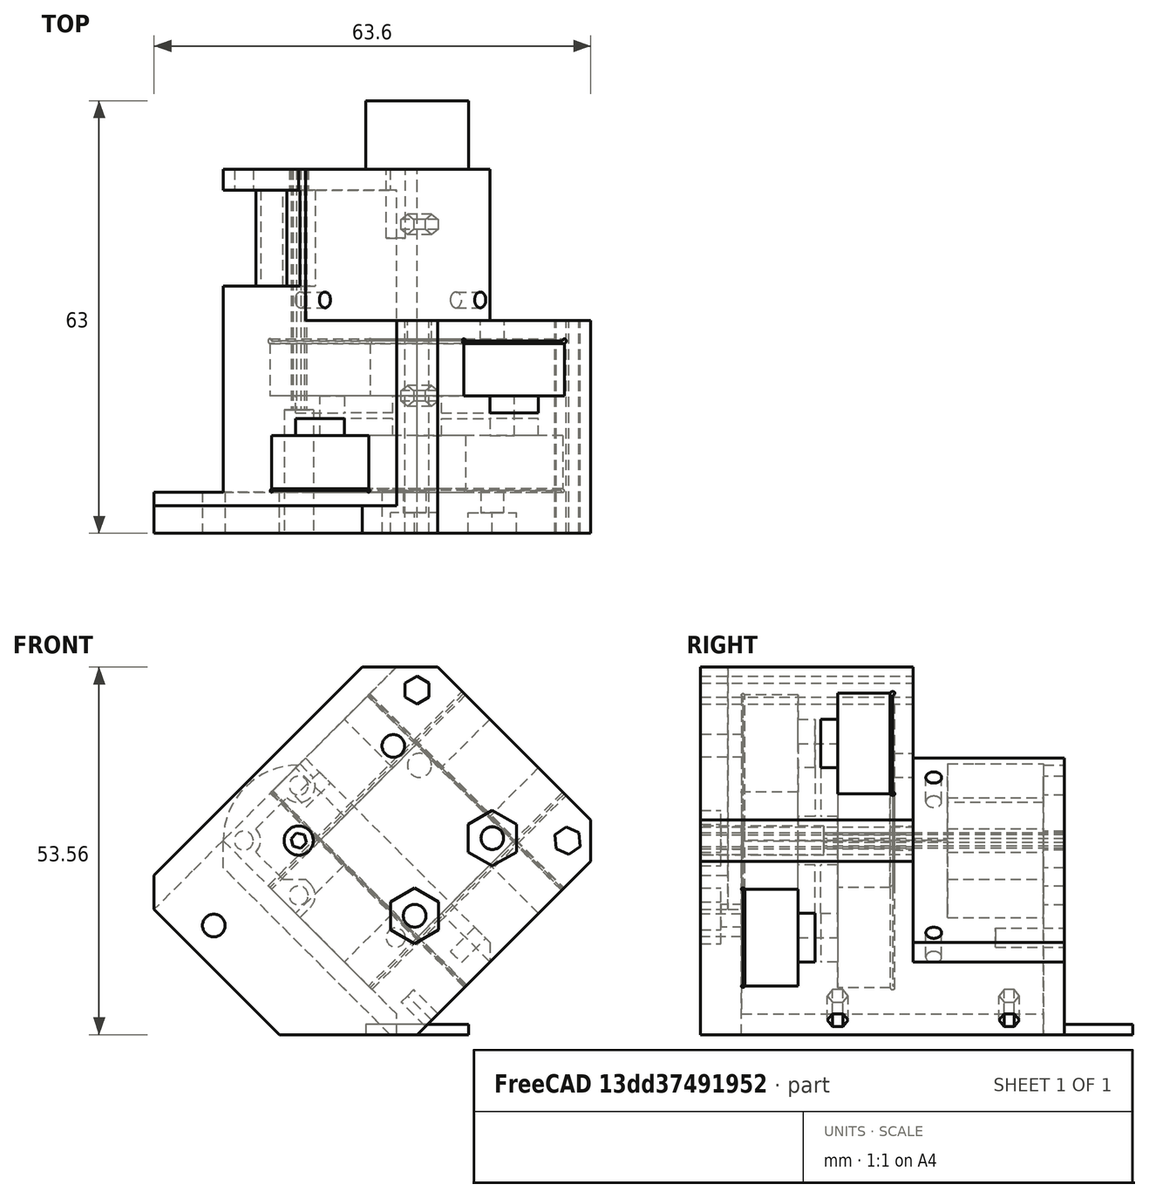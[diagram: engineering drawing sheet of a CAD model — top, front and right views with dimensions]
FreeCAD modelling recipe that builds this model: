
FCSTD DOCUMENT  (FreeCAD 0.19R)
Label: bottom
License: All rights reserved
LicenseURL: http://en.wikipedia.org/wiki/All_rights_reserved
objects: Sketcher::SketchObject×25, PartDesign::Pocket×18, PartDesign::Pad×5, PartDesign::Body×1, Mesh::Feature×1
note: 72 computed .brp shape members not serialized (recipe doc carries the construction recipe); baked Part::Feature solids carry a one-line shape summary decoded from their .brp

FEATURE [Sketcher::SketchObject] Sketch  label="Body001"
  FullyConstrained = true
  MapMode = 5
  Support = -> [XY_Plane]
  sketch-geometry (11):
    g0: LineSegment StartX=20 StartY=15.7574 StartZ=0 EndX=20 EndY=-15.7574 EndZ=0
    g1: LineSegment StartX=15.7574 StartY=-20 StartZ=0 EndX=-20 EndY=-20 EndZ=0
    g2: LineSegment StartX=-20 StartY=-15.7574 StartZ=0 EndX=-20 EndY=19.9515 EndZ=0
    g3: Circle CenterX=-12.1976 CenterY=12.1976 CenterZ=0 NormalX=0 NormalY=0 NormalZ=1 AngleXU=0 Radius=2.1
    g4: LineSegment StartX=-12.1976 StartY=12.1976 StartZ=0 EndX=0 EndY=0 EndZ=0
    g5: ArcOfCircle CenterX=-12.1976 CenterY=12.1976 CenterZ=0 NormalX=0 NormalY=0 NormalZ=1 AngleXU=0 Radius=11 StartAngle=0.788519 EndAngle=2.35931
    g6: LineSegment StartX=-4.44373 StartY=20 StartZ=0 EndX=15.7574 EndY=20 EndZ=0
    g7: LineSegment StartX=15.7574 StartY=-20 StartZ=0 EndX=20 EndY=-15.7574 EndZ=0
    g8: LineSegment StartX=-20 StartY=-15.7574 StartZ=0 EndX=-22.1213 EndY=-17.8787 EndZ=0
    g9: LineSegment StartX=-22.1213 StartY=-17.8787 StartZ=0 EndX=-20 EndY=-20 EndZ=0
    g10: LineSegment StartX=15.7574 StartY=20 StartZ=0 EndX=20 EndY=15.7574 EndZ=0
  constraints (32):
    c: Horizontal(g1)
    c: Vertical(g0)
    c: Vertical(g2)
    c: Distance(g-1,g3) = 17.25
    c: Coincident(g4,g3)
    c: Coincident(g4,g-1)
    c: Angle(g4) = -0.785398
    c: Diameter(g3) = 4.2
    c: Coincident(g5,g3)
    c: Diameter(g5) = 22
    c: DistanceX(g1) = -20
    c: Coincident(g6,g5)
    c: Horizontal(g6)
    c: Coincident(g5,g2)
    c: Coincident(g7,g1)
    c: Coincident(g7,g0)
    c: Angle(g7) = 0.785398
    c: Distance(g7) = 6
    c: DistanceY(g1) = -20
    c: Coincident(g2,g8)
    c: Coincident(g8,g9)
    c: Coincident(g9,g1)
    c: Angle(g9) = -0.785398
    c: Angle(g8) = -2.35619
    c: Distance(g9) = 3
    c: DistanceX(g2) = -20
    c: Coincident(g10,g6)
    c: Coincident(g10,g0)
    c: Distance(g10) = 6
    c: Angle(g10) = -0.785398
    c: DistanceX(g0) = 20
    c: DistanceY(g6) = 20
FEATURE [PartDesign::Pad] Pad
  Direction = (1,1,1)
  Length = 53
  Length2 = 10
  Profile = -> Sketch
  Reversed = true
  Type = 0
FEATURE [Sketcher::SketchObject] Sketch001  label="RailHole"
  FullyConstrained = true
  MapMode = 5
  Placement = pos=(20,0,0) rot=(0.57735,0.57735,0.57735;2.0944rad)
  Support = -> [Pad]
  sketch-geometry (10):
    g0: LineSegment StartX=-10.35 StartY=-27.65 StartZ=0 EndX=-10.35 EndY=-20 EndZ=0
    g1: LineSegment StartX=5 StartY=-17.5 StartZ=0 EndX=-5 EndY=-17.5 EndZ=0
    g2: LineSegment StartX=10 StartY=-28 StartZ=0 EndX=-10 EndY=-28 EndZ=0
    g3: LineSegment StartX=5 StartY=-17.5 StartZ=0 EndX=5 EndY=-20 EndZ=0
    g4: LineSegment StartX=-5 StartY=-20 StartZ=0 EndX=-5 EndY=-17.5 EndZ=0
    g5: LineSegment StartX=-10.35 StartY=-20 StartZ=0 EndX=-5 EndY=-20 EndZ=0
    g6: LineSegment StartX=5 StartY=-20 StartZ=0 EndX=10.3495 EndY=-20 EndZ=0
    g7: LineSegment StartX=10.3495 StartY=-27.65 StartZ=0 EndX=10.3495 EndY=-20 EndZ=0
    g8: ArcOfCircle CenterX=-10.35 CenterY=-28 CenterZ=0 NormalX=0 NormalY=0 NormalZ=1 AngleXU=0 Radius=0.35 StartAngle=1.5708 EndAngle=6.28319
    g9: ArcOfCircle CenterX=10.35 CenterY=-28 CenterZ=0 NormalX=0 NormalY=0 NormalZ=1 AngleXU=0 Radius=0.35 StartAngle=3.14159 EndAngle=7.85541
  constraints (29):
    c: Vertical(g0)
    c: Symmetric(g1,g1,g-2)
    c: Distance(g1) = 10
    c: Coincident(g1,g3)
    c: Vertical(g3)
    c: Coincident(g4,g1)
    c: Symmetric(g3,g4,g-2)
    c: Distance(g3) = 2.5
    c: Distance(g2) = 20
    c: Coincident(g5,g4)
    c: Horizontal(g5)
    c: Coincident(g3,g6)
    c: Horizontal(g6)
    c: Vertical(g7)
    c: Coincident(g0,g5)
    c: Coincident(g7,g6)
    c: Coincident(g0,g8)
    c: Coincident(g8,g2)
    c: Diameter(g8) = 0.7
    c: DistanceX(g0,g8) = 0
    c: DistanceY(g2,g8) = 0
    c: Coincident(g9,g2)
    c: Coincident(g9,g7)
    c: Diameter(g9) = 0.7
    c: DistanceY(g2,g9) = 0
    c: DistanceX(g7,g9) = 0.0005
    c: Symmetric(g9,g8,g-2)
    c: Distance(g9,g6) = 8
    c: DistanceY(g8) = -28
FEATURE [PartDesign::Pocket] Pocket
  BaseFeature = -> Pad
  Length = 5
  Length2 = 100
  Profile = -> Sketch001
  Type = 1
FEATURE [Sketcher::SketchObject] Sketch008  label="ExtruderHole"
  FullyConstrained = false
  MapMode = 5
  Placement = pos=(0,0,4) rot=(0,0,1;0rad)
  sketch-geometry (2):
    g0: LineSegment StartX=0 StartY=0 StartZ=0 EndX=-54.6242 EndY=54.6242 EndZ=0
    g1: Circle CenterX=-12.1976 CenterY=12.1976 CenterZ=0 NormalX=0 NormalY=0 NormalZ=1 AngleXU=0 Radius=0.75
  constraints (5):
    c: Coincident(g0,g-1)
    c: Angle(g0) = 2.35619
    c: PointOnObject(g1,g0)
    c: Distance(g-1,g1) = 17.25
    c: Diameter(g1) = 1.5
FEATURE [Sketcher::SketchObject] Sketch009  label="reference"
  FullyConstrained = false
  MapMode = 5
  Placement = pos=(0,0,-25) rot=(1,0,0;3.14159rad)
  sketch-geometry (2):
    g0: Circle CenterX=-12.0208 CenterY=-12.0208 CenterZ=0 NormalX=0 NormalY=0 NormalZ=1 AngleXU=0 Radius=10
    g1: LineSegment StartX=0 StartY=0 StartZ=0 EndX=-27.7674 EndY=-27.7674 EndZ=0
  constraints (5):
    c: Diameter(g0) = 20
    c: Coincident(g1,g-1)
    c: Angle(g1) = -2.35619
    c: PointOnObject(g0,g1)
    c: Distance(g0,g1) = 17
FEATURE [Sketcher::SketchObject] Sketch010  label="reference2"
  FullyConstrained = false
  MapMode = 5
  Placement = pos=(0,0,-37) rot=(1,0,0;3.14159rad)
  sketch-geometry (2):
    g0: Circle CenterX=-12.1976 CenterY=-12.1976 CenterZ=0 NormalX=0 NormalY=0 NormalZ=1 AngleXU=0 Radius=8
    g1: LineSegment StartX=0 StartY=0 StartZ=0 EndX=-38.1566 EndY=-38.1566 EndZ=0
  constraints (5):
    c: Diameter(g0) = 16
    c: Coincident(g1,g-1)
    c: Angle(g1) = -2.35619
    c: Distance(g0,g1) = 17.25
    c: PointOnObject(g0,g1)
FEATURE [Sketcher::SketchObject] Sketch021  label="InternalTri"
  FullyConstrained = true
  MapMode = 5
  Placement = pos=(0,-3e-15,-12) rot=(0,0,1;0rad)
  sketch-geometry (4):
    g0: LineSegment StartX=-10 StartY=10 StartZ=0 EndX=10 EndY=10 EndZ=0
    g1: LineSegment StartX=10 StartY=10 StartZ=0 EndX=10 EndY=-10 EndZ=0
    g2: LineSegment StartX=10 StartY=-10 StartZ=0 EndX=-10 EndY=-10 EndZ=0
    g3: LineSegment StartX=-10 StartY=-10 StartZ=0 EndX=-10 EndY=10 EndZ=0
  constraints (11):
    c: Coincident(g0,g1)
    c: Coincident(g1,g2)
    c: Coincident(g2,g3)
    c: Coincident(g3,g0)
    c: Horizontal(g0)
    c: Horizontal(g2)
    c: Vertical(g1)
    c: Vertical(g3)
    c: Symmetric(g1,g0,g-1)
    c: Equal(g1,g0)
    c: Distance(g1) = 20
FEATURE [PartDesign::Pocket] Pocket002
  BaseFeature = -> Pocket
  Length = 10
  Length2 = 2
  Profile = -> Sketch021
  Type = 4
FEATURE [Sketcher::SketchObject] Sketch019  label="RailHole2"
  FullyConstrained = true
  MapMode = 5
  Placement = pos=(0,-20,0) rot=(1,0,0;1.5708rad)
  Support = -> [Pocket002]
  sketch-geometry (10):
    g0: LineSegment StartX=-9.75 StartY=-6.2 StartZ=0 EndX=9.75 EndY=-6.2 EndZ=0
    g1: LineSegment StartX=10 StartY=-14.2 StartZ=0 EndX=5 EndY=-14.2 EndZ=0
    g2: LineSegment StartX=5 StartY=-14.2 StartZ=0 EndX=5 EndY=-16.7 EndZ=0
    g3: LineSegment StartX=5 StartY=-16.7 StartZ=0 EndX=-5 EndY=-16.7 EndZ=0
    g4: LineSegment StartX=-5 StartY=-16.7 StartZ=0 EndX=-5 EndY=-14.2 EndZ=0
    g5: LineSegment StartX=-5 StartY=-14.2 StartZ=0 EndX=-10 EndY=-14.2 EndZ=0
    g6: ArcOfCircle CenterX=10 CenterY=-6.2 CenterZ=0 NormalX=0 NormalY=0 NormalZ=1 AngleXU=0 Radius=0.25 StartAngle=4.71239 EndAngle=9.42478
    g7: ArcOfCircle CenterX=-10 CenterY=-6.2 CenterZ=0 NormalX=0 NormalY=0 NormalZ=1 AngleXU=0 Radius=0.25 StartAngle=-9e-16 EndAngle=4.71239
    g8: LineSegment StartX=-10 StartY=-14.2 StartZ=0 EndX=-10 EndY=-6.45 EndZ=0
    g9: LineSegment StartX=10 StartY=-14.2 StartZ=0 EndX=10 EndY=-6.45 EndZ=0
  constraints (29):
    c: Horizontal(g0)
    c: Horizontal(g1)
    c: Coincident(g1,g2)
    c: Vertical(g2)
    c: Coincident(g2,g3)
    c: Horizontal(g3)
    c: Coincident(g3,g4)
    c: Vertical(g4)
    c: Coincident(g4,g5)
    c: Symmetric(g1,g5,g-2)
    c: Distance(g3) = 10
    c: Symmetric(g4,g1,g-2)
    c: DistanceY(g0) = -6.2
    c: Distance(g2) = 2.5
    c: Coincident(g6,g0)
    c: Coincident(g7,g0)
    c: Distance(g7,g6) = 20
    c: DistanceY(g1,g6) = 8
    c: Coincident(g8,g5)
    c: Vertical(g8)
    c: Coincident(g9,g1)
    c: Coincident(g9,g6)
    c: Vertical(g9)
    c: Coincident(g7,g8)
    c: Symmetric(g6,g7,g-2)
    c: Diameter(g6) = 0.5
    c: Equal(g6,g7)
    c: DistanceX(g7,g7) = 0
    c: DistanceY(g7,g0) = 0
FEATURE [Sketcher::SketchObject] Sketch024  label="hgxLITEholes"
  FullyConstrained = false
  MapMode = 5
  Placement = pos=(0,0,4) rot=(0,0,1;0rad)
  sketch-geometry (5):
    g0: Circle CenterX=7.30241 CenterY=12.1976 CenterZ=0 NormalX=0 NormalY=0 NormalZ=1 AngleXU=0 Radius=1.65
    g1: Circle CenterX=-29.6976 CenterY=12.1976 CenterZ=0 NormalX=0 NormalY=0 NormalZ=1 AngleXU=0 Radius=1.65
    g2: LineSegment StartX=-29.6976 StartY=12.1976 StartZ=0 EndX=7.30241 EndY=12.1976 EndZ=0
    g3: LineSegment StartX=0 StartY=0 StartZ=0 EndX=-27.1729 EndY=27.1729 EndZ=0
    g4: Circle CenterX=-12.1976 CenterY=12.1976 CenterZ=0 NormalX=0 NormalY=0 NormalZ=1 AngleXU=0 Radius=1.0154
  constraints (12):
    c: Diameter(g0) = 3.3
    c: Equal(g0,g1)
    c: Coincident(g2,g1)
    c: Coincident(g2,g0)
    c: Distance(g2) = 37
    c: Coincident(g3,g-1)
    c: Angle(g3) = 2.35619
    c: PointOnObject(g4,g3)
    c: Distance(g-1,g4) = 17.25
    c: Distance(g4,g0) = 19.5
    c: Horizontal(g2)
    c: PointOnObject(g4,g2)
FEATURE [PartDesign::Pocket] Pocket003
  BaseFeature = -> Pocket002
  Length = 5
  Length2 = 100
  Profile = -> Sketch019
  Type = 1
FEATURE [Sketcher::SketchObject] Sketch026  label="BottomSculp"
  FullyConstrained = false
  MapMode = 5
  Placement = pos=(0,0,-53) rot=(1,0,0;3.14159rad)
  Support = -> [Pocket003]
  sketch-geometry (5):
    g0: LineSegment StartX=29.4648 StartY=27.8981 StartZ=0 EndX=28.2209 EndY=-23.4245 EndZ=0
    g1: LineSegment StartX=28.2209 StartY=-23.4245 StartZ=0 EndX=-3.00001 EndY=-23.4245 EndZ=0
    g2: LineSegment StartX=-3.00001 StartY=-23.4245 StartZ=0 EndX=-3 EndY=18 EndZ=0
    g3: LineSegment StartX=-3 StartY=18 StartZ=0 EndX=-14.2101 EndY=29.2101 EndZ=0
    g4: LineSegment StartX=-14.2101 StartY=29.2101 StartZ=0 EndX=29.4648 EndY=27.8981 EndZ=0
  constraints (11):
    c: Coincident(g0,g1)
    c: Horizontal(g1)
    c: Coincident(g1,g2)
    c: Angle(g2) = 1.5708
    c: Coincident(g2,g3)
    c: Angle(g3) = 2.35619
    c: Coincident(g4,g3)
    c: Coincident(g4,g0)
    c: DistanceY(g2) = 18
    c: DistanceX(g2) = -3
    c: Angle(g3) = 2.35619
FEATURE [PartDesign::Pocket] Pocket004
  BaseFeature = -> Pocket003
  Length = 22
  Length2 = 100
  Profile = -> Sketch026
  Type = 0
FEATURE [Sketcher::SketchObject] Sketch004  label="Yboltpattern"
  FullyConstrained = true
  MapMode = 5
  Placement = pos=(0,0,-31) rot=(1,0,0;3.14159rad)
  Support = -> [Pocket004]
  sketch-geometry (8):
    g0: Circle CenterX=-8 CenterY=7.5 CenterZ=0 NormalX=0 NormalY=0 NormalZ=1 AngleXU=0 Radius=1.75
    g1: Circle CenterX=8 CenterY=7.5 CenterZ=0 NormalX=0 NormalY=0 NormalZ=1 AngleXU=0 Radius=1.75
    g2: Circle CenterX=-8 CenterY=-7.5 CenterZ=0 NormalX=0 NormalY=0 NormalZ=1 AngleXU=0 Radius=1.75
    g3: Circle CenterX=8 CenterY=-7.5 CenterZ=0 NormalX=0 NormalY=0 NormalZ=1 AngleXU=0 Radius=1.75
    g4: LineSegment StartX=-8 StartY=7.5 StartZ=0 EndX=8 EndY=7.5 EndZ=0
    g5: LineSegment StartX=8 StartY=7.5 StartZ=0 EndX=8 EndY=-7.5 EndZ=0
    g6: LineSegment StartX=8 StartY=-7.5 StartZ=0 EndX=-8 EndY=-7.5 EndZ=0
    g7: LineSegment StartX=-8 StartY=-7.5 StartZ=0 EndX=-8 EndY=7.5 EndZ=0
  constraints (18):
    c: Diameter(g0) = 3.5
    c: Equal(g0,g1)
    c: Equal(g0,g2)
    c: Equal(g0,g3)
    c: Distance(g2,g0) = 15
    c: Distance(g3,g2) = 16
    c: Coincident(g4,g0)
    c: Coincident(g4,g1)
    c: Coincident(g4,g5)
    c: Coincident(g5,g3)
    c: Coincident(g5,g6)
    c: Coincident(g6,g2)
    c: Coincident(g6,g7)
    c: Coincident(g7,g4)
    c: Equal(g5,g7)
    c: Equal(g4,g6)
    c: Symmetric(g1,g2,g-1)
    c: Symmetric(g0,g1,g-2)
FEATURE [Sketcher::SketchObject] Sketch022  label="VoronHoleRelif"
  FullyConstrained = true
  MapMode = 5
  Placement = pos=(0,0,-28) rot=(0,0,1;0rad)
  Support = -> [Pocket004]
  sketch-geometry (11):
    g0: ArcOfCircle CenterX=-17.8884 CenterY=6.52425 CenterZ=0 NormalX=0 NormalY=0 NormalZ=1 AngleXU=0 Radius=2.4 StartAngle=4.71239 EndAngle=6.28319
    g1: ArcOfCircle CenterX=-6.58192 CenterY=17.8307 CenterZ=0 NormalX=0 NormalY=0 NormalZ=1 AngleXU=0 Radius=2.4 StartAngle=3.14159 EndAngle=6.28319
    g2: LineSegment StartX=-22.2684 StartY=4.12425 StartZ=0 EndX=-17.8884 EndY=4.12425 EndZ=0
    g3: LineSegment StartX=-22.2684 StartY=23.8307 StartZ=0 EndX=-4.18192 EndY=23.8307 EndZ=0
    g4: LineSegment StartX=-4.18192 StartY=23.8307 StartZ=0 EndX=-4.18192 EndY=17.8307 EndZ=0
    g5: LineSegment StartX=-22.2684 StartY=4.12425 StartZ=0 EndX=-22.2684 EndY=23.8307 EndZ=0
    g6: ArcOfCircle CenterX=-17.8172 CenterY=17.8307 CenterZ=0 NormalX=0 NormalY=0 NormalZ=1 AngleXU=0 Radius=2.4 StartAngle=4.71239 EndAngle=6.28319
    g7: LineSegment StartX=-15.4172 StartY=17.8307 StartZ=0 EndX=-8.98192 EndY=17.8307 EndZ=0
    g8: LineSegment StartX=-17.8172 StartY=9.85307 StartZ=0 EndX=-15.4884 EndY=7.52425 EndZ=0
    g9: LineSegment StartX=-15.4884 StartY=6.52425 StartZ=0 EndX=-15.4884 EndY=7.52425 EndZ=0
    g10: LineSegment StartX=-17.8172 StartY=9.85307 StartZ=0 EndX=-17.8172 EndY=15.4307 EndZ=0
  constraints (33):
    c: Horizontal(g2)
    c: Coincident(g3,g4)
    c: Tangent(g4,g1) = 1.5708
    c: Tangent(g2,g0) = -1.5708
    c: Diameter(g0) = 4.8
    c: Equal(g0,g1)
    c: Vertical(g4)
    c: Horizontal(g3)
    c: Coincident(g5,g2)
    c: Coincident(g5,g3)
    c: Vertical(g5)
    c: Distance(g2) = 4.38
    c: Distance(g4) = 6
    c: DistanceX(g1) = -6.58192
    c: DistanceY(g1) = 17.8307
    c: DistanceX(g0) = -17.8884
    c: DistanceY(g0) = 6.52425
    c: Coincident(g7,g6)
    c: Coincident(g7,g1)
    c: Horizontal(g7)
    c: Perpendicular(g1,g7)
    c: Diameter(g6) = 4.8
    c: Perpendicular(g6,g7)
    c: Angle(g8) = -0.785398
    c: Vertical(g9)
    c: Tangent(g9,g0) = -1.5708
    c: Distance(g9) = 1
    c: Coincident(g8,g9)
    c: Coincident(g10,g8)
    c: Coincident(g10,g6)
    c: Vertical(g10)
    c: Perpendicular(g6,g10)
    c: DistanceX(g6) = -17.8172
FEATURE [PartDesign::Pocket] Pocket005
  BaseFeature = -> Pocket004
  Length = 22
  Length2 = -8
  Profile = -> Sketch022
  Type = 4
FEATURE [Sketcher::SketchObject] Sketch017  label="VoronHoles3"
  FullyConstrained = true
  MapMode = 5
  Placement = pos=(0,0,-50) rot=(0,0,1;0rad)
  Support = -> [Pocket005]
  sketch-geometry (10):
    g0: Circle CenterX=-6.54074 CenterY=17.8544 CenterZ=0 NormalX=0 NormalY=0 NormalZ=1 AngleXU=0 Radius=1.375
    g1: Circle CenterX=-17.8544 CenterY=6.54074 CenterZ=0 NormalX=0 NormalY=0 NormalZ=1 AngleXU=0 Radius=1.375
    g2: Circle CenterX=-6.54074 CenterY=6.54074 CenterZ=0 NormalX=0 NormalY=0 NormalZ=1 AngleXU=0 Radius=1.375
    g3: Circle CenterX=-17.8544 CenterY=17.8544 CenterZ=0 NormalX=0 NormalY=0 NormalZ=1 AngleXU=0 Radius=1.375
    g4: LineSegment StartX=-6.54074 StartY=17.8544 StartZ=0 EndX=-6.54074 EndY=6.54074 EndZ=0
    g5: LineSegment StartX=-6.54074 StartY=6.54074 StartZ=0 EndX=-17.8544 EndY=6.54074 EndZ=0
    g6: LineSegment StartX=-17.8544 StartY=6.54074 StartZ=0 EndX=-17.8544 EndY=17.8544 EndZ=0
    g7: LineSegment StartX=-17.8544 StartY=17.8544 StartZ=0 EndX=-6.54074 EndY=17.8544 EndZ=0
    g8: LineSegment StartX=0 StartY=0 StartZ=0 EndX=-37.1726 EndY=37.1726 EndZ=0
    g9: Circle CenterX=-12.1976 CenterY=12.1976 CenterZ=0 NormalX=0 NormalY=0 NormalZ=1 AngleXU=0 Radius=0.77
  constraints (25):
    c: Coincident(g4,g0)
    c: Coincident(g4,g2)
    c: Coincident(g4,g5)
    c: Coincident(g5,g1)
    c: Coincident(g5,g6)
    c: Coincident(g6,g3)
    c: Coincident(g6,g7)
    c: Coincident(g7,g4)
    c: Equal(g4,g7)
    c: Equal(g7,g6)
    c: Equal(g6,g5)
    c: Coincident(g8,g-1)
    c: PointOnObject(g9,g8)
    c: Distance(g-1,g9) = 17.25
    c: Diameter(g1) = 2.75
    c: Equal(g1,g3)
    c: Equal(g1,g0)
    c: Equal(g1,g2)
    c: Symmetric(g0,g1,g9)
    c: Distance(g2,g3) = 16
    c: Angle(g8) = 2.35619
    c: PointOnObject(g2,g8)
    c: Perpendicular(g7,g4)
    c: Distance(g8) = 52.57
    c: Diameter(g9) = 1.54
FEATURE [PartDesign::Pocket] Pocket006
  BaseFeature = -> Pocket005
  Length = 5
  Length2 = 100
  Profile = -> Sketch017
  Type = 1
FEATURE [Sketcher::SketchObject] Sketch025  label="FanDuctMountHole"
  FullyConstrained = true
  MapMode = 5
  Placement = pos=(0,0,-53) rot=(1,0,0;3.14159rad)
  Support = -> [Pocket006]
  sketch-geometry (1):
    g0: Circle CenterX=-12.2 CenterY=7.8 CenterZ=0 NormalX=0 NormalY=0 NormalZ=1 AngleXU=0 Radius=1.4
  constraints (3):
    c: Diameter(g0) = 2.8
    c: DistanceX(g0) = -12.2
    c: DistanceY(g0) = 7.8
FEATURE [PartDesign::Pocket] Pocket007
  BaseFeature = -> Pocket006
  Length = 10
  Length2 = 100
  Profile = -> Sketch025
  Type = 0
FEATURE [PartDesign::Pocket] Pocket008
  BaseFeature = -> Pocket007
  Length = 9
  Length2 = 100
  Profile = -> Sketch004
  Type = 0
FEATURE [Sketcher::SketchObject] Sketch007  label="ExtruderPlatform"
  ExternalGeometry = -> [Pad]
  FullyConstrained = false
  MapMode = 5
  Support = -> [Pocket008]
  sketch-geometry (12):
    g0: LineSegment StartX=-20 StartY=-20 StartZ=0 EndX=15.7574 EndY=-20 EndZ=0
    g1: LineSegment StartX=0 StartY=0 StartZ=0 EndX=-70.7107 EndY=70.7107 EndZ=0
    g2: Circle CenterX=-12.1976 CenterY=12.1976 CenterZ=0 NormalX=0 NormalY=0 NormalZ=1 AngleXU=0 Radius=2.125
    g3: LineSegment StartX=15.7574 StartY=-20 StartZ=0 EndX=20 EndY=-15.7574 EndZ=0
    g4: LineSegment StartX=20 StartY=-15.7574 StartZ=0 EndX=20 EndY=15.7574 EndZ=0
    g5: LineSegment StartX=20 StartY=15.7574 StartZ=0 EndX=15.7574 EndY=20 EndZ=0
    g6: LineSegment StartX=-20 StartY=-20 StartZ=0 EndX=-34.1976 EndY=-5.80241 EndZ=0
    g7: LineSegment StartX=-12.1976 StartY=-100 StartZ=0 EndX=-12.1976 EndY=100 EndZ=0
    g8: LineSegment StartX=-34.1976 StartY=-5.80241 StartZ=0 EndX=-34.1976 EndY=20 EndZ=0
    g9: LineSegment StartX=-34.1976 StartY=20 StartZ=0 EndX=15.7574 EndY=20 EndZ=0
    g10: Circle CenterX=-29.6976 CenterY=12.1976 CenterZ=0 NormalX=0 NormalY=0 NormalZ=1 AngleXU=0 Radius=1.4
    g11: Circle CenterX=7.30241 CenterY=11.9057 CenterZ=0 NormalX=0 NormalY=0 NormalZ=1 AngleXU=0 Radius=1.4
  constraints (35):
    c: Coincident(g1,g-1)
    c: Angle(g1) = 2.35619
    c: Diameter(g2) = 4.25
    c: PointOnObject(g2,g1)
    c: Distance(g-1,g2) = 17.25
    c: Coincident(g0,g3)
    c: Coincident(g3,g4)
    c: Coincident(g6,g0)
    c: Angle(g6) = 2.35619
    c: Coincident(g5,g4)
    c: Distance(g1) = 100
    c: PointOnObject(g2,g7)
    c: DistanceX(g0,g0) = -35.7574
    c: DistanceY(g0,g0) = 0
    c: DistanceX(g3,g0) = -40
    c: DistanceY(g3,g0) = -4.24264
    c: DistanceX(g4) = 20
    c: DistanceY(g4) = 15.7574
    c: DistanceX(g3) = 20
    c: DistanceY(g3) = -15.7574
    c: Coincident(g8,g6)
    c: Vertical(g8)
    c: Horizontal(g9)
    c: Coincident(g5,g9)
    c: Distance(g8,g7) = 22
    c: DistanceX(g5) = 15.7574
    c: DistanceY(g5) = 20
    c: Symmetric(g7,g7,g-1)
    c: Distance(g7) = 200
    c: DistanceX(g10,g2) = 17.5
    c: DistanceX(g2,g11) = 19.5
    c: Diameter(g10) = 2.8
    c: Equal(g10,g11)
    c: DistanceY(g10,g2) = 0
    c: Coincident(g9,g8)
FEATURE [PartDesign::Pad] Pad001
  BaseFeature = -> Pocket008
  Direction = (1,1,1)
  Length = 6
  Length2 = 100
  Profile = -> Sketch007
  Reversed = true
  Type = 0
FEATURE [PartDesign::Pocket] Pocket009
  BaseFeature = -> Pad001
  Length = 11
  Length2 = 100
  Profile = -> Sketch024
  Type = 0
FEATURE [PartDesign::Pocket] Pocket010
  BaseFeature = -> Pocket009
  Length = 5
  Length2 = 100
  Profile = -> Sketch008
  Type = 1
FEATURE [Sketcher::SketchObject] Sketch003  label="Xboltpattern"
  FullyConstrained = true
  MapMode = 5
  Support = -> [Pocket010]
  sketch-geometry (8):
    g0: Circle CenterX=-8 CenterY=7.5 CenterZ=0 NormalX=0 NormalY=0 NormalZ=1 AngleXU=0 Radius=1.65
    g1: Circle CenterX=8 CenterY=7.5 CenterZ=0 NormalX=0 NormalY=0 NormalZ=1 AngleXU=0 Radius=1.65
    g2: Circle CenterX=-8 CenterY=-7.5 CenterZ=0 NormalX=0 NormalY=0 NormalZ=1 AngleXU=0 Radius=1.65
    g3: Circle CenterX=8 CenterY=-7.5 CenterZ=0 NormalX=0 NormalY=0 NormalZ=1 AngleXU=0 Radius=1.65
    g4: LineSegment StartX=-8 StartY=7.5 StartZ=0 EndX=8 EndY=7.5 EndZ=0
    g5: LineSegment StartX=8 StartY=7.5 StartZ=0 EndX=8 EndY=-7.5 EndZ=0
    g6: LineSegment StartX=8 StartY=-7.5 StartZ=0 EndX=-8 EndY=-7.5 EndZ=0
    g7: LineSegment StartX=-8 StartY=-7.5 StartZ=0 EndX=-8 EndY=7.5 EndZ=0
  constraints (19):
    c: Diameter(g0) = 3.3
    c: Equal(g0,g1)
    c: Equal(g0,g2)
    c: Equal(g0,g3)
    c: Distance(g0,g1) = 16
    c: Distance(g1,g3) = 15
    c: Coincident(g4,g0)
    c: Coincident(g4,g1)
    c: Horizontal(g4)
    c: Coincident(g4,g5)
    c: Coincident(g5,g3)
    c: Vertical(g5)
    c: Coincident(g5,g6)
    c: Coincident(g6,g2)
    c: Coincident(g6,g7)
    c: Coincident(g7,g4)
    c: Symmetric(g2,g1,g-1)
    c: Equal(g7,g5)
    c: Equal(g6,g4)
FEATURE [Sketcher::SketchObject] Sketch029  label="Adhesion"
  FullyConstrained = false
  MapMode = 5
  Placement = pos=(0,0,-53) rot=(1,0,0;3.14159rad)
  sketch-geometry (4):
    g0: LineSegment StartX=-13.636 StartY=24.2426 StartZ=0 EndX=-24.2426 EndY=13.636 EndZ=0
    g1: LineSegment StartX=-24.2426 StartY=13.636 StartZ=0 EndX=-25.3033 EndY=14.6967 EndZ=0
    g2: LineSegment StartX=-25.3033 StartY=14.6967 StartZ=0 EndX=-14.6967 EndY=25.3033 EndZ=0
    g3: LineSegment StartX=-14.6967 StartY=25.3033 StartZ=0 EndX=-13.636 EndY=24.2426 EndZ=0
  constraints (10):
    c: Coincident(g0,g1)
    c: Coincident(g1,g2)
    c: Coincident(g2,g3)
    c: Coincident(g3,g0)
    c: Angle(g2) = 0.785398
    c: Distance(g2) = 15
    c: Distance(g1) = 1.5
    c: Distance(g3) = 1.5
    c: Perpendicular(g2,g3)
    c: Perpendicular(g2,g1)
FEATURE [Sketcher::SketchObject] Sketch033  label="WireMgmnt"
  FullyConstrained = true
  MapMode = 5
  Placement = pos=(0,-20,0) rot=(1,0,0;1.5708rad)
  sketch-geometry (14):
    g0: LineSegment StartX=-15.7 StartY=-20.7506 StartZ=0 EndX=-15.7 EndY=-19.2494 EndZ=0
    g1: LineSegment StartX=-15.7 StartY=-19.2494 StartZ=0 EndX=-17 EndY=-18.4989 EndZ=0
    g2: LineSegment StartX=-17 StartY=-18.4989 StartZ=0 EndX=-18.3 EndY=-19.2494 EndZ=0
    g3: LineSegment StartX=-18.3 StartY=-19.2494 StartZ=0 EndX=-18.3 EndY=-20.7506 EndZ=0
    g4: LineSegment StartX=-18.3 StartY=-20.7506 StartZ=0 EndX=-17 EndY=-21.5011 EndZ=0
    g5: LineSegment StartX=-17 StartY=-21.5011 StartZ=0 EndX=-15.7 EndY=-20.7506 EndZ=0
    g6: Circle CenterX=-17 CenterY=-20 CenterZ=0 NormalX=0 NormalY=0 NormalZ=1 AngleXU=0 Radius=1.50111
    g7: LineSegment StartX=-15.7 StartY=-44.2494 StartZ=0 EndX=-17 EndY=-43.4989 EndZ=0
    g8: LineSegment StartX=-17 StartY=-43.4989 StartZ=0 EndX=-18.3 EndY=-44.2494 EndZ=0
    g9: LineSegment StartX=-18.3 StartY=-44.2494 StartZ=0 EndX=-18.3 EndY=-45.7506 EndZ=0
    g10: LineSegment StartX=-18.3 StartY=-45.7506 StartZ=0 EndX=-17 EndY=-46.5011 EndZ=0
    g11: LineSegment StartX=-17 StartY=-46.5011 StartZ=0 EndX=-15.7 EndY=-45.7506 EndZ=0
    g12: LineSegment StartX=-15.7 StartY=-45.7506 StartZ=0 EndX=-15.7 EndY=-44.2494 EndZ=0
    g13: Circle CenterX=-17 CenterY=-45 CenterZ=0 NormalX=0 NormalY=0 NormalZ=1 AngleXU=0 Radius=1.50111
  constraints (34):
    c: Coincident(g0,g1)
    c: Coincident(g1,g2)
    c: Coincident(g2,g3)
    c: Coincident(g3,g4)
    c: Coincident(g4,g5)
    c: Coincident(g5,g0)
    c: Equal(g0, g1-g5) x5
    c: PointOnObject(g0,g6)
    c: PointOnObject(g1,g6)
    c: PointOnObject(g2,g6)
    c: PointOnObject(g3,g6)
    c: PointOnObject(g4,g6)
    c: PointOnObject(g5,g6)
    c: Coincident(g7,g8)
    c: Coincident(g8,g9)
    c: Coincident(g9,g10)
    c: Coincident(g10,g11)
    c: Coincident(g11,g12)
    c: Coincident(g12,g7)
    c: Equal(g7, g8-g12) x5
    c: PointOnObject(g7,g13)
    c: PointOnObject(g8,g13)
    c: PointOnObject(g9,g13)
    c: PointOnObject(g10,g13)
    c: PointOnObject(g11,g13)
    c: PointOnObject(g12,g13)
    c: DistanceX(g13) = -17
    c: Distance(g10,g7) = 2.6
    c: Vertical(g9)
    c: DistanceY(g13) = -45
    c: Distance(g3,g0) = 2.6
    c: DistanceY(g6) = -20
    c: Vertical(g3)
    c: DistanceX(g6) = -17
FEATURE [Sketcher::SketchObject] Sketch035  label="Bottom Reinforce"
  FullyConstrained = false
  MapMode = 5
  Placement = pos=(0,0,-53) rot=(1,0,0;3.14159rad)
  sketch-geometry (4):
    g0: LineSegment StartX=-22.779 StartY=17.221 StartZ=0 EndX=-22.779 EndY=-17.1725 EndZ=0
    g1: LineSegment StartX=-22.779 StartY=-17.1725 StartZ=0 EndX=-20 EndY=-19.9515 EndZ=0
    g2: LineSegment StartX=-20 StartY=-19.9515 StartZ=0 EndX=-20 EndY=20 EndZ=0
    g3: LineSegment StartX=-20 StartY=20 StartZ=0 EndX=-22.779 EndY=17.221 EndZ=0
  constraints (9):
    c: Vertical(g0)
    c: Coincident(g0,g1)
    c: Coincident(g1,g2)
    c: Vertical(g2)
    c: Coincident(g2,g3)
    c: Coincident(g3,g0)
    c: Angle(g1) = -0.785398
    c: DistanceY(g2) = 20
    c: Angle(g3) = -2.35619
FEATURE [Sketcher::SketchObject] Sketch037  label="BumpTrim"
  FullyConstrained = false
  MapMode = 5
  sketch-geometry (4):
    g0: LineSegment StartX=-26.2848 StartY=31.2083 StartZ=0 EndX=-1.26106 EndY=31.2083 EndZ=0
    g1: LineSegment StartX=-1.26106 StartY=31.2083 StartZ=0 EndX=-1.26106 EndY=20 EndZ=0
    g2: LineSegment StartX=-1.26106 StartY=20 StartZ=0 EndX=-26.2848 EndY=20 EndZ=0
    g3: LineSegment StartX=-26.2848 StartY=20 StartZ=0 EndX=-26.2848 EndY=31.2083 EndZ=0
  constraints (9):
    c: Coincident(g0,g1)
    c: Coincident(g1,g2)
    c: Coincident(g2,g3)
    c: Coincident(g3,g0)
    c: Horizontal(g0)
    c: Horizontal(g2)
    c: Vertical(g1)
    c: Vertical(g3)
    c: DistanceY(g1) = 20
FEATURE [PartDesign::Pocket] Pocket011
  BaseFeature = -> Pocket010
  Length = 10
  Length2 = 100
  Profile = -> Sketch003
  Type = 0
FEATURE [Sketcher::SketchObject] Sketch036  label="countersink"
  FullyConstrained = true
  MapMode = 5
  Support = -> [Pocket011]
  sketch-geometry (14):
    g0: LineSegment StartX=11.9037 StartY=-8.546 StartZ=0 EndX=10.8577 EndY=-4.64226 EndZ=0
    g1: LineSegment StartX=10.8577 StartY=-4.64226 StartZ=0 EndX=6.954 EndY=-3.59626 EndZ=0
    g2: LineSegment StartX=6.954 StartY=-3.59626 StartZ=0 EndX=4.09626 EndY=-6.454 EndZ=0
    g3: LineSegment StartX=4.09626 StartY=-6.454 StartZ=0 EndX=5.14226 EndY=-10.3577 EndZ=0
    g4: LineSegment StartX=5.14226 StartY=-10.3577 StartZ=0 EndX=9.046 EndY=-11.4037 EndZ=0
    g5: LineSegment StartX=9.046 StartY=-11.4037 StartZ=0 EndX=11.9037 EndY=-8.546 EndZ=0
    g6: Circle CenterX=8 CenterY=-7.5 CenterZ=0 NormalX=0 NormalY=0 NormalZ=1 AngleXU=0 Radius=4.04145
    g7: LineSegment StartX=-5.14226 StartY=-4.64226 StartZ=0 EndX=-9.046 EndY=-3.59626 EndZ=0
    g8: LineSegment StartX=-9.046 StartY=-3.59626 StartZ=0 EndX=-11.9037 EndY=-6.454 EndZ=0
    g9: LineSegment StartX=-11.9037 StartY=-6.454 StartZ=0 EndX=-10.8577 EndY=-10.3577 EndZ=0
    g10: LineSegment StartX=-10.8577 StartY=-10.3577 StartZ=0 EndX=-6.954 EndY=-11.4037 EndZ=0
    g11: LineSegment StartX=-6.954 StartY=-11.4037 StartZ=0 EndX=-4.09626 EndY=-8.546 EndZ=0
    g12: LineSegment StartX=-4.09626 StartY=-8.546 StartZ=0 EndX=-5.14226 EndY=-4.64226 EndZ=0
    g13: Circle CenterX=-8 CenterY=-7.5 CenterZ=0 NormalX=0 NormalY=0 NormalZ=1 AngleXU=0 Radius=4.04145
  constraints (34):
    c: Coincident(g0,g1)
    c: Coincident(g1,g2)
    c: Coincident(g2,g3)
    c: Coincident(g3,g4)
    c: Coincident(g4,g5)
    c: Coincident(g5,g0)
    c: Equal(g0, g1-g5) x5
    c: PointOnObject(g0,g6)
    c: PointOnObject(g1,g6)
    c: PointOnObject(g2,g6)
    c: PointOnObject(g3,g6)
    c: PointOnObject(g4,g6)
    c: PointOnObject(g5,g6)
    c: Coincident(g7,g8)
    c: Coincident(g8,g9)
    c: Coincident(g9,g10)
    c: Coincident(g10,g11)
    c: Coincident(g11,g12)
    c: Coincident(g12,g7)
    c: Equal(g7, g8-g12) x5
    c: PointOnObject(g7,g13)
    c: PointOnObject(g8,g13)
    c: PointOnObject(g9,g13)
    c: PointOnObject(g10,g13)
    c: PointOnObject(g11,g13)
    c: PointOnObject(g12,g13)
    c: Angle(g11) = 0.785398
    c: Angle(g5) = 0.785398
    c: Distance(g0,g2) = 7
    c: Distance(g7,g8) = 7
    c: DistanceX(g6) = 8
    c: DistanceY(g6) = -7.5
    c: DistanceY(g13) = -7.5
    c: DistanceX(g13) = -8
FEATURE [PartDesign::Pocket] Pocket012
  BaseFeature = -> Pocket011
  Length = 3
  Length2 = 100
  Profile = -> Sketch036
  Type = 0
FEATURE [PartDesign::Pocket] Pocket013
  BaseFeature = -> Pocket012
  Length = 5
  Length2 = 100
  Profile = -> Sketch033
  Type = 0
FEATURE [PartDesign::Pad] Pad002
  BaseFeature = -> Pocket013
  Direction = (1,1,1)
  Length = 3
  Length2 = 100
  Profile = -> Sketch035
  Reversed = true
  Type = 0
FEATURE [PartDesign::Pocket] Pocket014
  BaseFeature = -> Pad002
  Length = 40
  Length2 = 100
  Profile = -> Sketch037
  Type = 0
FEATURE [PartDesign::Pad] Pad003
  BaseFeature = -> Pocket014
  Direction = (1,1,1)
  Length = 10
  Length2 = 100
  Profile = -> Sketch029
  Type = 0
FEATURE [Sketcher::SketchObject] Sketch039  label="platformBump"
  ExternalGeometry = -> [Pad003]
  FullyConstrained = true
  MapMode = 5
  Support = -> [Pad003]
  sketch-geometry (4):
    g0: LineSegment StartX=-30.6621 StartY=23.5355 StartZ=0 EndX=12.2218 EndY=23.5355 EndZ=0
    g1: LineSegment StartX=12.2218 StartY=23.5355 StartZ=0 EndX=15.7574 EndY=20 EndZ=0
    g2: LineSegment StartX=15.7574 StartY=20 StartZ=0 EndX=-34.1976 EndY=20 EndZ=0
    g3: LineSegment StartX=-34.1976 StartY=20 StartZ=0 EndX=-30.6621 EndY=23.5355 EndZ=0
  constraints (10):
    c: Coincident(g0,g1)
    c: Coincident(g1,g2)
    c: Coincident(g2,g3)
    c: Coincident(g3,g0)
    c: Horizontal(g0)
    c: Distance(g1) = 5
    c: Coincident(g2,g-3)
    c: Coincident(g1,g-4)
    c: Angle(g1) = -0.785398
    c: Angle(g3) = 0.785398
FEATURE [PartDesign::Pad] Pad004
  BaseFeature = -> Pad003
  Direction = (1,1,1)
  Length = 4
  Length2 = 100
  Profile = -> Sketch039
  Reversed = true
  Type = 0
FEATURE [Sketcher::SketchObject] Sketch040  label="WireHoles"
  FullyConstrained = true
  MapMode = 5
  Support = -> [Pad004]
  sketch-geometry (21):
    g0: LineSegment StartX=16.1911 StartY=-17.3989 StartZ=0 EndX=17.49 EndY=-15.8509 EndZ=0
    g1: LineSegment StartX=17.49 StartY=-15.8509 StartZ=0 EndX=16.7989 EndY=-13.952 EndZ=0
    g2: LineSegment StartX=16.7989 StartY=-13.952 StartZ=0 EndX=14.8089 EndY=-13.6011 EndZ=0
    g3: LineSegment StartX=14.8089 StartY=-13.6011 StartZ=0 EndX=13.51 EndY=-15.1491 EndZ=0
    g4: LineSegment StartX=13.51 StartY=-15.1491 StartZ=0 EndX=14.2011 EndY=-17.048 EndZ=0
    g5: LineSegment StartX=14.2011 StartY=-17.048 StartZ=0 EndX=16.1911 EndY=-17.3989 EndZ=0
    g6: Circle CenterX=15.5 CenterY=-15.5 CenterZ=0 NormalX=0 NormalY=0 NormalZ=1 AngleXU=0 Radius=2.02073
    g7: LineSegment StartX=14.977 StartY=17.4519 StartZ=0 EndX=13.5481 EndY=16.023 EndZ=0
    g8: LineSegment StartX=13.5481 StartY=16.023 StartZ=0 EndX=14.0711 EndY=14.0711 EndZ=0
    g9: LineSegment StartX=14.0711 StartY=14.0711 StartZ=0 EndX=16.023 EndY=13.5481 EndZ=0
    g10: LineSegment StartX=16.023 StartY=13.5481 StartZ=0 EndX=17.4519 EndY=14.977 EndZ=0
    g11: LineSegment StartX=17.4519 StartY=14.977 StartZ=0 EndX=16.9289 EndY=16.9289 EndZ=0
    g12: LineSegment StartX=16.9289 StartY=16.9289 StartZ=0 EndX=14.977 EndY=17.4519 EndZ=0
    g13: Circle CenterX=15.5 CenterY=15.5 CenterZ=0 NormalX=0 NormalY=0 NormalZ=1 AngleXU=0 Radius=2.02073
    g14: LineSegment StartX=-14.7753 StartY=-17.2247 StartZ=0 EndX=-14.327 EndY=-15.5517 EndZ=0
    g15: LineSegment StartX=-14.327 StartY=-15.5517 StartZ=0 EndX=-15.5517 EndY=-14.327 EndZ=0
    g16: LineSegment StartX=-15.5517 StartY=-14.327 StartZ=0 EndX=-17.2247 EndY=-14.7753 EndZ=0
    g17: LineSegment StartX=-17.2247 StartY=-14.7753 StartZ=0 EndX=-17.673 EndY=-16.4483 EndZ=0
    g18: LineSegment StartX=-17.673 StartY=-16.4483 StartZ=0 EndX=-16.4483 EndY=-17.673 EndZ=0
    g19: LineSegment StartX=-16.4483 StartY=-17.673 StartZ=0 EndX=-14.7753 EndY=-17.2247 EndZ=0
    g20: Circle CenterX=-16 CenterY=-16 CenterZ=0 NormalX=0 NormalY=0 NormalZ=1 AngleXU=0 Radius=1.73205
  constraints (51):
    c: Coincident(g0,g1)
    c: Coincident(g1,g2)
    c: Coincident(g2,g3)
    c: Coincident(g3,g4)
    c: Coincident(g4,g5)
    c: Coincident(g5,g0)
    c: Equal(g0, g1-g5) x5
    c: PointOnObject(g0,g6)
    c: PointOnObject(g1,g6)
    c: PointOnObject(g2,g6)
    c: PointOnObject(g3,g6)
    c: PointOnObject(g4,g6)
    c: PointOnObject(g5,g6)
    c: Coincident(g7,g8)
    c: Coincident(g8,g9)
    c: Coincident(g9,g10)
    c: Coincident(g10,g11)
    c: Coincident(g11,g12)
    c: Coincident(g12,g7)
    c: Equal(g7, g8-g12) x5
    c: PointOnObject(g7,g13)
    c: PointOnObject(g8,g13)
    c: PointOnObject(g9,g13)
    c: PointOnObject(g10,g13)
    c: PointOnObject(g11,g13)
    c: PointOnObject(g12,g13)
    c: Distance(g0,g4) = 3.5
    c: Distance(g7,g11) = 3.5
    c: DistanceX(g13) = 15.5
    c: DistanceY(g13) = 15.5
    c: DistanceX(g6) = 15.5
    c: DistanceY(g6) = -15.5
    c: Coincident(g14,g15)
    c: Coincident(g15,g16)
    c: Coincident(g16,g17)
    c: Coincident(g17,g18)
    c: Coincident(g18,g19)
    c: Coincident(g19,g14)
    c: Equal(g14, g15-g19) x5
    c: PointOnObject(g14,g20)
    c: PointOnObject(g15,g20)
    c: PointOnObject(g16,g20)
    c: PointOnObject(g17,g20)
    c: PointOnObject(g18,g20)
    c: PointOnObject(g19,g20)
    c: Distance(g18,g14) = 3
    c: Angle(g15) = 2.35619
    c: DistanceX(g20) = -16
    c: DistanceY(g20) = -16
    c: Angle(g3) = -2.26893
    c: Angle(g11) = 1.8326
FEATURE [PartDesign::Pocket] Pocket015
  BaseFeature = -> Pad004
  Length = 5
  Length2 = 100
  Profile = -> Sketch040
  Type = 1
FEATURE [Sketcher::SketchObject] Sketch041  label="PCBmountholes"
  FullyConstrained = true
  MapMode = 5
  Placement = pos=(-3.00001,-9.80387e-07,0) rot=(0.57735,0.57735,0.57735;2.0944rad)
  Support = -> [Pocket015]
  sketch-geometry (2):
    g0: Circle CenterX=16 CenterY=-34 CenterZ=0 NormalX=0 NormalY=0 NormalZ=1 AngleXU=0 Radius=1.15
    g1: Circle CenterX=-16 CenterY=-34 CenterZ=0 NormalX=0 NormalY=0 NormalZ=1 AngleXU=0 Radius=1.15
  constraints (5):
    c: Distance(g0,g1) = 32
    c: Symmetric(g1,g0,g-2)
    c: Diameter(g0) = 2.3
    c: Equal(g0,g1)
    c: DistanceY(g1) = -34
FEATURE [PartDesign::Pocket] Pocket016
  BaseFeature = -> Pocket015
  Length = 5
  Length2 = 100
  Profile = -> Sketch041
  Type = 0
FEATURE [Sketcher::SketchObject] Sketch042
  FullyConstrained = true
  MapMode = 5
  Placement = pos=(0,0,-53) rot=(1,0,0;3.14159rad)
  Support = -> [Pocket014]
  sketch-geometry (7):
    g0: LineSegment StartX=-13.3547 StartY=-12.2 StartZ=0 EndX=-12.7774 EndY=-13.2 EndZ=0
    g1: LineSegment StartX=-12.7774 StartY=-13.2 StartZ=0 EndX=-11.6226 EndY=-13.2 EndZ=0
    g2: LineSegment StartX=-11.6226 StartY=-13.2 StartZ=0 EndX=-11.0453 EndY=-12.2 EndZ=0
    g3: LineSegment StartX=-11.0453 StartY=-12.2 StartZ=0 EndX=-11.6226 EndY=-11.2 EndZ=0
    g4: LineSegment StartX=-11.6226 StartY=-11.2 StartZ=0 EndX=-12.7774 EndY=-11.2 EndZ=0
    g5: LineSegment StartX=-12.7774 StartY=-11.2 StartZ=0 EndX=-13.3547 EndY=-12.2 EndZ=0
    g6: Circle CenterX=-12.2 CenterY=-12.2 CenterZ=0 NormalX=0 NormalY=0 NormalZ=1 AngleXU=0 Radius=1.1547
  constraints (17):
    c: Coincident(g0,g1)
    c: Coincident(g1,g2)
    c: Coincident(g2,g3)
    c: Coincident(g3,g4)
    c: Coincident(g4,g5)
    c: Coincident(g5,g0)
    c: Equal(g0, g1-g5) x5
    c: PointOnObject(g0,g6)
    c: PointOnObject(g1,g6)
    c: PointOnObject(g2,g6)
    c: PointOnObject(g3,g6)
    c: PointOnObject(g4,g6)
    c: PointOnObject(g5,g6)
    c: DistanceX(g6) = -12.2
    c: DistanceY(g6) = -12.2
    c: Distance(g0,g4) = 2
    c: Angle(g1) = 0
FEATURE [PartDesign::Pocket] Pocket017
  BaseFeature = -> Pocket016
  Length = 5
  Length2 = 100
  Profile = -> Sketch042
  Type = 1
FEATURE [Sketcher::SketchObject] Sketch043
  FullyConstrained = true
  MapMode = 5
  Support = -> [Pocket017]
  sketch-geometry (1):
    g0: Circle CenterX=-12.2 CenterY=12.2 CenterZ=0 NormalX=0 NormalY=0 NormalZ=1 AngleXU=0 Radius=2.125
  constraints (3):
    c: DistanceX(g0) = -12.2
    c: DistanceY(g0) = 12.2
    c: Diameter(g0) = 4.25
FEATURE [PartDesign::Pocket] Pocket018
  BaseFeature = -> Pocket017
  Length = 18
  Length2 = 100
  Profile = -> Sketch043
  Type = 0
FEATURE [PartDesign::Body] Body
  Group = -> [Sketch,Pad,Sketch001,Pocket,Sketch003,Sketch004,Sketch007,Sketch008,Sketch009,Sketch010,Sketch017,Sketch019,Sketch021,Pocket002,Sketch022,Sketch024,Sketch025,Sketch026,Pocket003,Pocket004,Pocket005,Pocket006,Pocket007,Pocket008,Pad001,Pocket009,Pocket010,Sketch029,Sketch033,Sketch035,Sketch036,Sketch037,Pocket011,Pocket012,Pocket013,Pad002,Pocket014,Pad003,Sketch039,Pad004,Sketch040,Pocket015,+6 more]
  Origin = -> Origin
  Placement = pos=(0,0,0) rot=(0.862856,-0.357407,0.357407;1.71777rad)
  Tip = -> Pocket018
FEATURE [Mesh::Feature] Mesh  label="Pocket018 (Meshed)"
